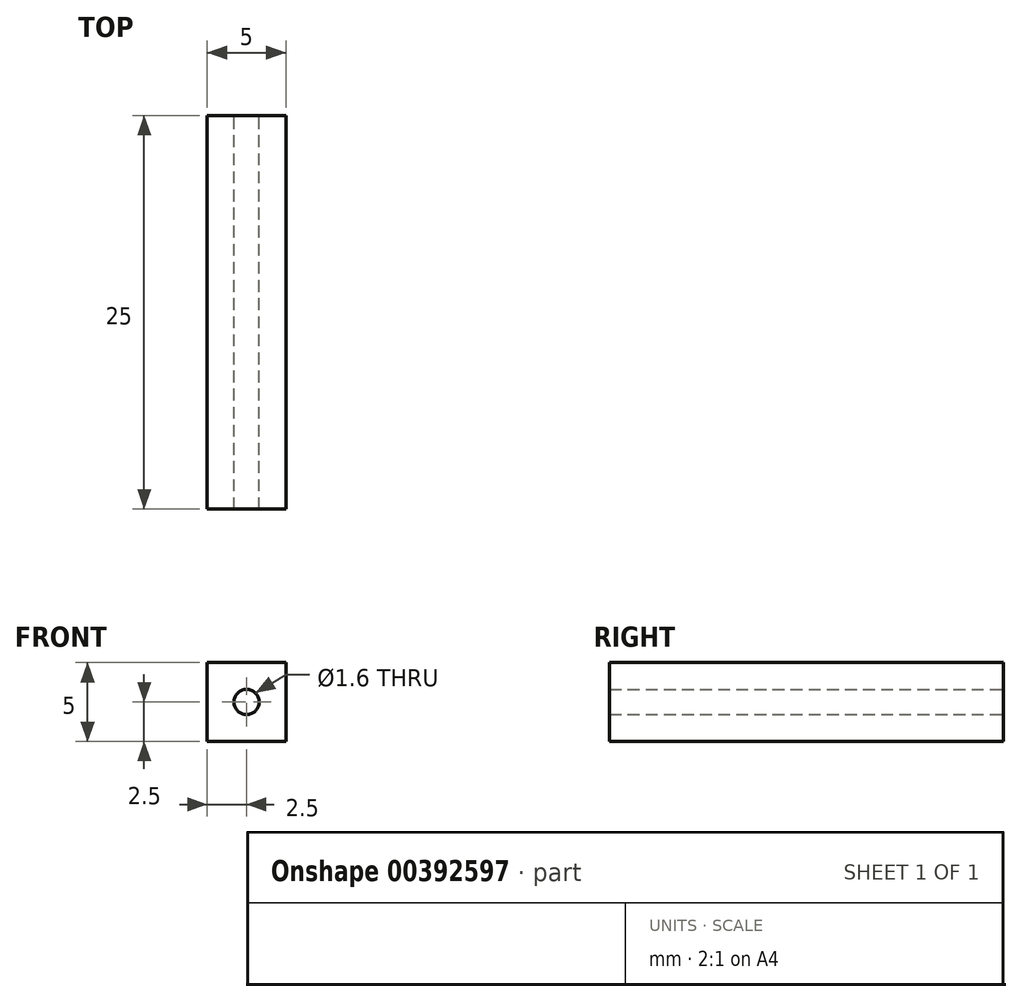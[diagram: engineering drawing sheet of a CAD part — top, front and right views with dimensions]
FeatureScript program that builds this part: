
annotation { "Feature Type Name" : "Feature", "Feature Type Description" : "" }
export const myFeature = defineFeature(function(context is Context, id is Id, definition is map)
    precondition{}
    {
        {
            var Q0;
            Q0=qCreatedBy(makeId("Front.planeOp"),FACE);
            var sketch = newSketch(context, id + "F0", { "sketchPlane" : qUnion([Q0])});
            skLineSegment(sketch, "E0.bottom", {"start": v(0, 0) * mm, "end": v(5, 0) * mm});
            skLineSegment(sketch, "E0.top", {"start": v(0, 5) * mm, "end": v(5, 5) * mm});
            skLineSegment(sketch, "E0.left", {"start": v(0, 0) * mm, "end": v(0, 5) * mm});
            skLineSegment(sketch, "E0.right", {"start": v(5, 0) * mm, "end": v(5, 5) * mm});
            skCircle(sketch, "E1", {"center": v(2.5, 2.5) * mm, "radius": 0.8 * mm});
            skSolve(sketch);
        }
        {
            var Q0;
            Q0=makeQuery(id+"F0.imprint","IMPRINT",FACE,{"disambiguationData":[TD([[makeQuery(id+"F0.imprint","IMPRINT",EDGE,{"derivedFrom":sQuery(id+"F0.wireOp",EDGE,"E0.bottom")}),1.0]])]});
            extrude(context, id + "F1", {"entities" : qUnion([Q0]), "depth" : 25 * mm});
        }
    });
